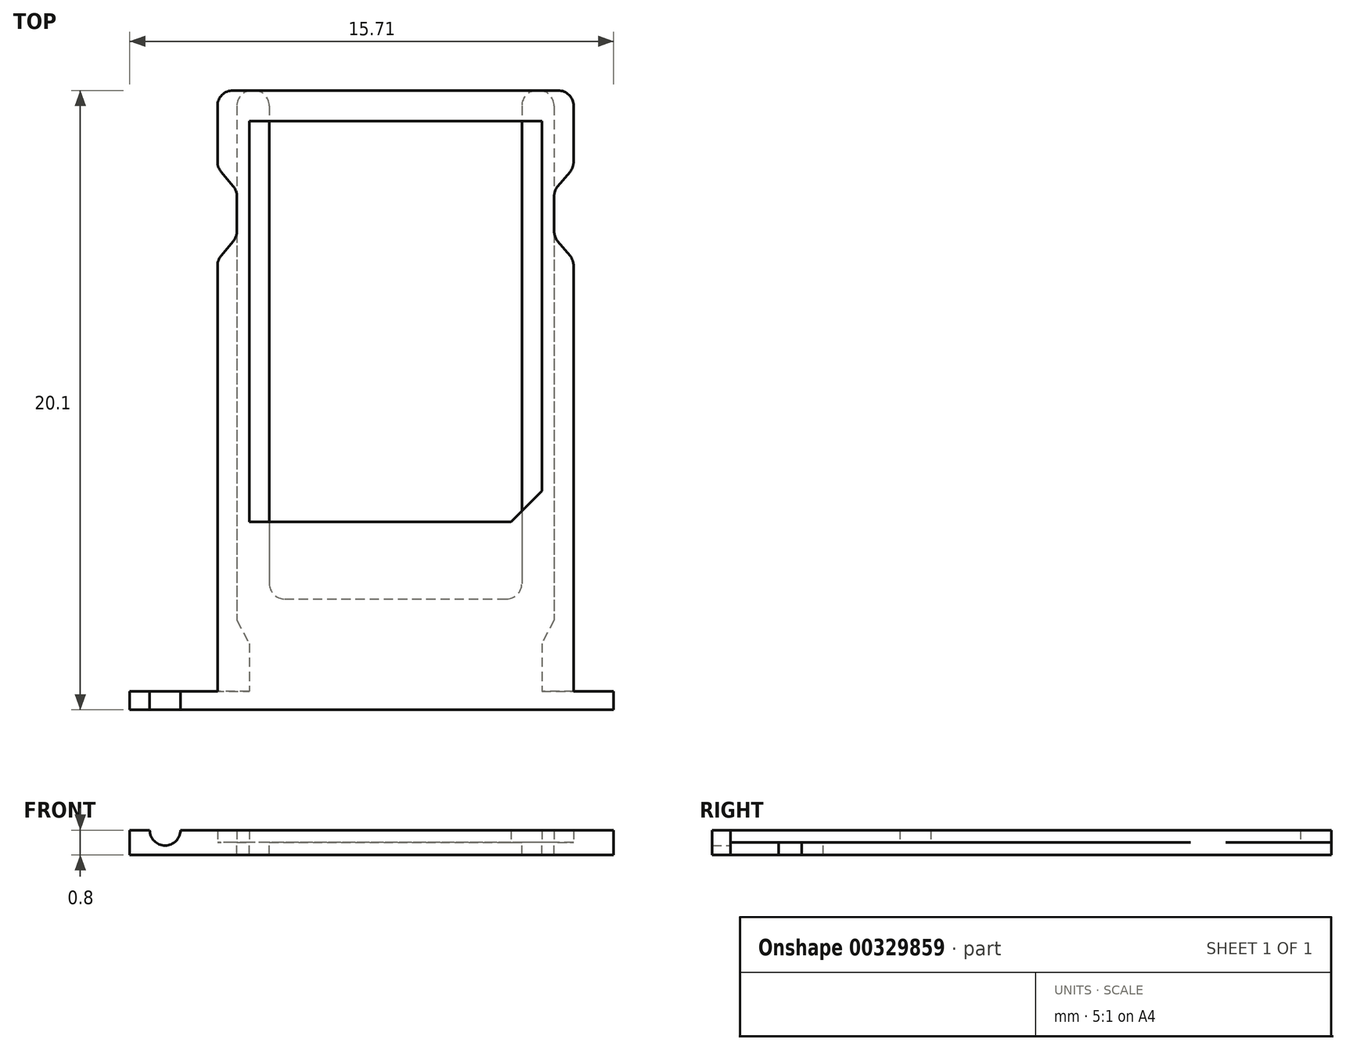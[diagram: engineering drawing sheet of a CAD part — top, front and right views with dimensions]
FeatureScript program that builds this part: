
annotation { "Feature Type Name" : "Feature", "Feature Type Description" : "" }
export const myFeature = defineFeature(function(context is Context, id is Id, definition is map)
    precondition{}
    {
        {
            var Q0;
            Q0=qCreatedBy(makeId("Top.planeOp"),FACE);
            var sketch = newSketch(context, id + "F0", { "sketchPlane" : qUnion([Q0])});
            skLineSegment(sketch, "E0", {"start": v(0, 0) * mm, "end": v(0, 14) * mm});
            skLineSegment(sketch, "E1", {"start": v(0.63, 14.75) * mm, "end": v(0.63, 16.25) * mm});
            skLineSegment(sketch, "E2", {"start": v(0.63, 16.25) * mm, "end": v(0, 17) * mm});
            skLineSegment(sketch, "E3", {"start": v(0, 17) * mm, "end": v(0, 19.5) * mm});
            skLineSegment(sketch, "E4", {"start": v(0, 19.5) * mm, "end": v(5.78, 19.5) * mm});
            skLineSegment(sketch, "E5", {"start": v(5.78, 19.5) * mm, "end": v(5.78, 0) * mm, "construction": true});
            skLineSegment(sketch, "E6", {"start": v(5.78, 0) * mm, "end": v(0, 0) * mm});
            skLineSegment(sketch, "E7.MirrorCS", {"start": v(11.56, 19.5) * mm, "end": v(5.78, 19.5) * mm});
            skLineSegment(sketch, "E8.MirrorCS", {"start": v(11.56, 17) * mm, "end": v(11.56, 19.5) * mm});
            skLineSegment(sketch, "E9.MirrorCS", {"start": v(10.93, 16.25) * mm, "end": v(11.56, 17) * mm});
            skLineSegment(sketch, "E10.MirrorCS", {"start": v(10.93, 14.75) * mm, "end": v(10.93, 16.25) * mm});
            skLineSegment(sketch, "E11.MirrorCS", {"start": v(11.56, 14) * mm, "end": v(10.93, 14.75) * mm});
            skLineSegment(sketch, "E12.MirrorCS", {"start": v(11.56, 0) * mm, "end": v(11.56, 14) * mm});
            skLineSegment(sketch, "E13.MirrorCS", {"start": v(5.78, 0) * mm, "end": v(11.56, 0) * mm});
            skLineSegment(sketch, "E14", {"start": v(0, 14) * mm, "end": v(0.63, 14.75) * mm});
            skLineSegment(sketch, "E15.bottom", {"start": v(9.53, 5.5) * mm, "end": v(1.03, 5.5) * mm});
            skLineSegment(sketch, "E15.top", {"start": v(10.53, 18.5) * mm, "end": v(1.03, 18.5) * mm});
            skLineSegment(sketch, "E15.left", {"start": v(10.53, 6.5) * mm, "end": v(10.53, 18.5) * mm});
            skLineSegment(sketch, "E15.right", {"start": v(1.03, 5.5) * mm, "end": v(1.03, 18.5) * mm});
            skPoint(sketch, "E15.middle", {"position": v(5.78, 12) * mm});
            skLineSegment(sketch, "E16", {"start": v(9.53, 5.5) * mm, "end": v(10.53, 6.5) * mm});
            skLineSegment(sketch, "E17", {"start": v(9.53, 5.5) * mm, "end": v(10.53, 5.5) * mm, "construction": true});
            skLineSegment(sketch, "E18", {"start": v(10.53, 6.5) * mm, "end": v(10.53, 5.5) * mm, "construction": true});
            skSolve(sketch);
        }
        {
            var Q0;
            Q0=makeQuery(id+"F0.imprint","IMPRINT",FACE,{"disambiguationData":[TD([[makeQuery(id+"F0.imprint","IMPRINT",EDGE,{"derivedFrom":sQuery(id+"F0.wireOp",EDGE,"E0")}),-1.0]])]});
            extrude(context, id + "F1", {"entities" : qUnion([Q0]), "depth" : 0.4 * mm, "offsetDistance" : 25 * mm});
        }
        {
            var Q0;
            Q0=makeQuery(id+"F1.opExtrude","CAP_FACE",FACE,{"disambiguationData":[OSD([sQuery(id+"F0.wireOp",EDGE,"E0"),sQuery(id+"F0.wireOp",EDGE,"E1"),sQuery(id+"F0.wireOp",EDGE,"E2"),sQuery(id+"F0.wireOp",EDGE,"E3"),sQuery(id+"F0.wireOp",EDGE,"E4"),sQuery(id+"F0.wireOp",EDGE,"E6"),sQuery(id+"F0.wireOp",EDGE,"E7.MirrorCS"),sQuery(id+"F0.wireOp",EDGE,"E8.MirrorCS"),sQuery(id+"F0.wireOp",EDGE,"E9.MirrorCS"),sQuery(id+"F0.wireOp",EDGE,"E10.MirrorCS"),sQuery(id+"F0.wireOp",EDGE,"E11.MirrorCS"),sQuery(id+"F0.wireOp",EDGE,"E12.MirrorCS"),sQuery(id+"F0.wireOp",EDGE,"E13.MirrorCS"),sQuery(id+"F0.wireOp",EDGE,"E14"),sQuery(id+"F0.wireOp",EDGE,"E15.bottom"),sQuery(id+"F0.wireOp",EDGE,"E15.top"),sQuery(id+"F0.wireOp",EDGE,"E15.left"),sQuery(id+"F0.wireOp",EDGE,"E15.right"),sQuery(id+"F0.wireOp",EDGE,"E16")])],"isStart":true});
            var sketch = newSketch(context, id + "F2", { "sketchPlane" : qUnion([Q0])});
            skLineSegment(sketch, "E19", {"start": v(0.63, -19.5) * mm, "end": v(0.63, -2.3) * mm});
            skLineSegment(sketch, "E20", {"start": v(0.63, -2.3) * mm, "end": v(1.03, -1.56) * mm});
            skLineSegment(sketch, "E21", {"start": v(1.03, -1.56) * mm, "end": v(1.03, 0) * mm});
            skLineSegment(sketch, "E22", {"start": v(1.68, -19.5) * mm, "end": v(1.68, -3) * mm});
            skLineSegment(sketch, "E23", {"start": v(1.68, -3) * mm, "end": v(5.78, -3) * mm});
            skLineSegment(sketch, "E24", {"start": v(5.78, -3) * mm, "end": v(5.78, 0) * mm, "construction": true});
            skLineSegment(sketch, "E25", {"start": v(5.78, 0) * mm, "end": v(1.03, 0) * mm});
            skLineSegment(sketch, "E26", {"start": v(0.63, -19.5) * mm, "end": v(1.68, -19.5) * mm});
            skLineSegment(sketch, "E27.MirrorCS", {"start": v(9.88, -3) * mm, "end": v(5.78, -3) * mm});
            skLineSegment(sketch, "E28.MirrorCS", {"start": v(9.88, -19.5) * mm, "end": v(9.88, -3) * mm});
            skLineSegment(sketch, "E29.MirrorCS", {"start": v(10.93, -19.5) * mm, "end": v(9.88, -19.5) * mm});
            skLineSegment(sketch, "E30.MirrorCS", {"start": v(10.93, -19.5) * mm, "end": v(10.93, -2.3) * mm});
            skLineSegment(sketch, "E31.MirrorCS", {"start": v(10.93, -2.3) * mm, "end": v(10.53, -1.56) * mm});
            skLineSegment(sketch, "E32.MirrorCS", {"start": v(10.53, -1.56) * mm, "end": v(10.53, 0) * mm});
            skLineSegment(sketch, "E33.MirrorCS", {"start": v(5.78, 0) * mm, "end": v(10.53, 0) * mm});
            skSolve(sketch);
        }
        {
            var Q0;
            Q0 = qSketchRegion(id + "F2", true);
            extrude(context, id + "F3", {"entities" : qUnion([Q0]), "operationType" : NewBodyOperationType.ADD, "depth" : 0.4 * mm, "offsetDistance" : 25 * mm});
        }
        {
            var Q0;
            Q0=makeQuery(id+"F3.boolean.opBoolean","MERGE",FACE,{"derivedFrom":[makeQuery(id+"F1.opExtrude","SWEPT_FACE",FACE,{"disambiguationData":[OSD([sQuery(id+"F0.wireOp",EDGE,"E6"),sQuery(id+"F0.wireOp",EDGE,"E13.MirrorCS")])]}),makeQuery(id+"F3.opExtrude","SWEPT_FACE",FACE,{"disambiguationData":[OSD([sQuery(id+"F2.wireOp",EDGE,"8BKzJbkm-a4ZE-JBbJ-XGdl-3KBP26bkulz1")])]})]});
            var sketch = newSketch(context, id + "F4", { "sketchPlane" : qUnion([Q0])});
            skLineSegment(sketch, "E34.bottom", {"start": v(-2.85, 0.4) * mm, "end": v(-2.2, 0.4) * mm});
            skLineSegment(sketch, "E34.top", {"start": v(-2.85, -0.4) * mm, "end": v(12.86, -0.4) * mm});
            skLineSegment(sketch, "E34.left", {"start": v(-2.85, 0.4) * mm, "end": v(-2.85, -0.4) * mm});
            skLineSegment(sketch, "E34.right", {"start": v(12.86, 0.4) * mm, "end": v(12.86, -0.4) * mm});
            skArc(sketch, "E35", {"start": v(-2.2, 0.4) * mm, "mid": v(-1.7, -0.1) * mm, "end": v(-1.2, 0.4) * mm});
            skLineSegment(sketch, "E36.trimOffspring", {"start": v(-1.2, 0.4) * mm, "end": v(12.86, 0.4) * mm});
            skLineSegment(sketch, "E37", {"start": v(-2.2, 0.4) * mm, "end": v(-1.7, 0.4) * mm, "construction": true});
            skLineSegment(sketch, "E38", {"start": v(-1.7, 0.4) * mm, "end": v(-1.2, 0.4) * mm, "construction": true});
            skSolve(sketch);
        }
        {
            var Q0;
            Q0 = qSketchRegion(id + "F4", true);
            extrude(context, id + "F5", {"entities" : qUnion([Q0]), "operationType" : NewBodyOperationType.ADD, "depth" : 0.6 * mm, "offsetDistance" : 25 * mm});
        }
        {
            var Q0;
            Q0=makeQuery(id+"F1.opExtrude","SWEPT_EDGE",EDGE,{"disambiguationData":[OSD([sQuery(id+"F0.wireOp",EDGE,"E7.MirrorCS"),sQuery(id+"F0.wireOp",EDGE,"E8.MirrorCS")])]});
            var Q1;
            Q1=makeQuery(id+"F1.opExtrude","SWEPT_EDGE",EDGE,{"disambiguationData":[OSD([sQuery(id+"F0.wireOp",EDGE,"E8.MirrorCS"),sQuery(id+"F0.wireOp",EDGE,"E9.MirrorCS")])]});
            var Q2;
            Q2=makeQuery(id+"F1.opExtrude","SWEPT_EDGE",EDGE,{"disambiguationData":[OSD([sQuery(id+"F0.wireOp",EDGE,"E9.MirrorCS"),sQuery(id+"F0.wireOp",EDGE,"E10.MirrorCS")])]});
            var Q3;
            Q3=makeQuery(id+"F1.opExtrude","SWEPT_EDGE",EDGE,{"disambiguationData":[OSD([sQuery(id+"F0.wireOp",EDGE,"E10.MirrorCS"),sQuery(id+"F0.wireOp",EDGE,"E11.MirrorCS")])]});
            var Q4;
            Q4=makeQuery(id+"F1.opExtrude","SWEPT_EDGE",EDGE,{"disambiguationData":[OSD([sQuery(id+"F0.wireOp",EDGE,"E11.MirrorCS"),sQuery(id+"F0.wireOp",EDGE,"E12.MirrorCS")])]});
            var Q5;
            Q5=makeQuery(id+"F1.opExtrude","SWEPT_EDGE",EDGE,{"disambiguationData":[OSD([sQuery(id+"F0.wireOp",EDGE,"E3"),sQuery(id+"F0.wireOp",EDGE,"E4")])]});
            var Q6;
            Q6=makeQuery(id+"F1.opExtrude","SWEPT_EDGE",EDGE,{"disambiguationData":[OSD([sQuery(id+"F0.wireOp",EDGE,"E2"),sQuery(id+"F0.wireOp",EDGE,"E3")])]});
            var Q7;
            Q7=makeQuery(id+"F1.opExtrude","SWEPT_EDGE",EDGE,{"disambiguationData":[OSD([sQuery(id+"F0.wireOp",EDGE,"E1"),sQuery(id+"F0.wireOp",EDGE,"E2")])]});
            var Q8;
            Q8=makeQuery(id+"F1.opExtrude","SWEPT_EDGE",EDGE,{"disambiguationData":[OSD([sQuery(id+"F0.wireOp",EDGE,"E0"),sQuery(id+"F0.wireOp",EDGE,"E14")])]});
            var Q9;
            Q9=makeQuery(id+"F1.opExtrude","SWEPT_EDGE",EDGE,{"disambiguationData":[OSD([sQuery(id+"F0.wireOp",EDGE,"E1"),sQuery(id+"F0.wireOp",EDGE,"E14")])]});
            var Q10;
            Q10=makeQuery(id+"F3.opExtrude","SWEPT_EDGE",EDGE,{"disambiguationData":[OSD([sQuery(id+"F2.wireOp",EDGE,"E27.MirrorCS"),sQuery(id+"F2.wireOp",EDGE,"E28.MirrorCS")])]});
            var Q11;
            Q11=makeQuery(id+"F3.opExtrude","SWEPT_EDGE",EDGE,{"disambiguationData":[OSD([sQuery(id+"F2.wireOp",EDGE,"E22"),sQuery(id+"F2.wireOp",EDGE,"E23")])]});
            var Q12;
            Q12=makeQuery(id+"F3.opExtrude","SWEPT_EDGE",EDGE,{"disambiguationData":[OSD([sQuery(id+"F0.wireOp",EDGE,"E4"),sQuery(id+"F0.wireOp",EDGE,"E7.MirrorCS"),sQuery(id+"F2.wireOp",EDGE,"E29.MirrorCS"),sQuery(id+"F2.wireOp",EDGE,"E30.MirrorCS")])]});
            var Q13;
            Q13=makeQuery(id+"F3.opExtrude","SWEPT_EDGE",EDGE,{"disambiguationData":[OSD([sQuery(id+"F0.wireOp",EDGE,"E4"),sQuery(id+"F0.wireOp",EDGE,"E7.MirrorCS"),sQuery(id+"F2.wireOp",EDGE,"E28.MirrorCS"),sQuery(id+"F2.wireOp",EDGE,"E29.MirrorCS")])]});
            var Q14;
            Q14=makeQuery(id+"F3.opExtrude","SWEPT_EDGE",EDGE,{"disambiguationData":[OSD([sQuery(id+"F0.wireOp",EDGE,"E4"),sQuery(id+"F0.wireOp",EDGE,"E7.MirrorCS"),sQuery(id+"F2.wireOp",EDGE,"E22"),sQuery(id+"F2.wireOp",EDGE,"E26")])]});
            var Q15;
            Q15=makeQuery(id+"F3.opExtrude","SWEPT_EDGE",EDGE,{"disambiguationData":[OSD([sQuery(id+"F0.wireOp",EDGE,"E4"),sQuery(id+"F0.wireOp",EDGE,"E7.MirrorCS"),sQuery(id+"F2.wireOp",EDGE,"E19"),sQuery(id+"F2.wireOp",EDGE,"E26")])]});
            var Q16;
            Q16=makeQuery(id+"F3.opExtrude","SWEPT_EDGE",EDGE,{"disambiguationData":[OSD([sQuery(id+"F0.wireOp",EDGE,"E6"),sQuery(id+"F0.wireOp",EDGE,"E13.MirrorCS"),sQuery(id+"F2.wireOp",EDGE,"E32.MirrorCS"),sQuery(id+"F2.wireOp",EDGE,"E33.MirrorCS")])]});
            var Q17;
            Q17=makeQuery(id+"F3.opExtrude","SWEPT_EDGE",EDGE,{"disambiguationData":[OSD([sQuery(id+"F0.wireOp",EDGE,"E6"),sQuery(id+"F0.wireOp",EDGE,"E13.MirrorCS"),sQuery(id+"F2.wireOp",EDGE,"E21"),sQuery(id+"F2.wireOp",EDGE,"E25")])]});
            fillet(context, id + "F6", {"entities" : qUnion([Q0, Q1, Q2, Q3, Q4, Q5, Q6, Q7, Q8, Q9, Q10, Q11, Q12, Q13, Q14, Q15, Q16, Q17]), "radius" : 0.5 * mm, "tangentPropagation" : true, "allowEdgeOverflow" : false});
        }
    });
